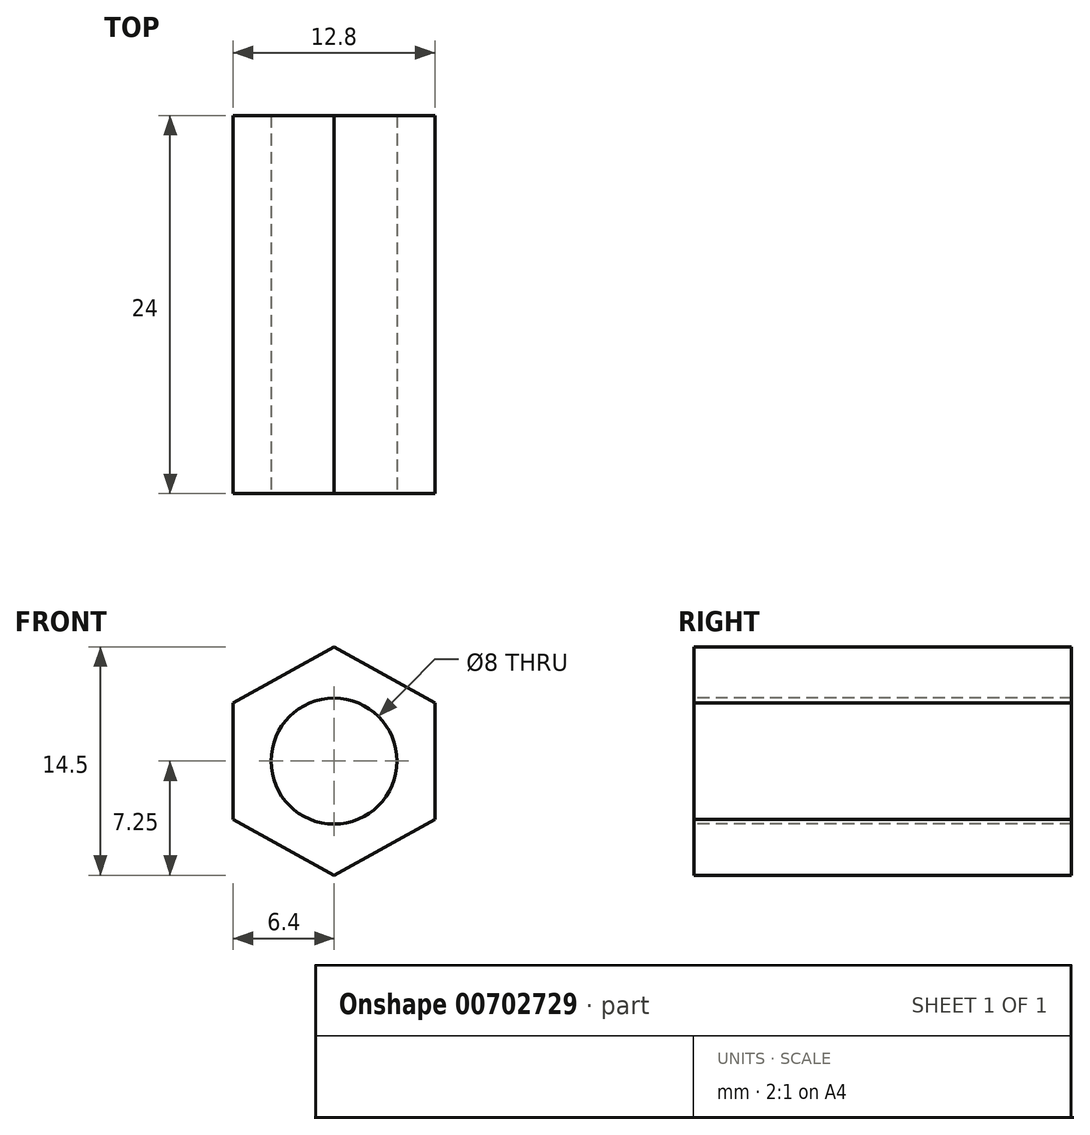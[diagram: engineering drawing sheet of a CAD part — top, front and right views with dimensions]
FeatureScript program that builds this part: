
annotation { "Feature Type Name" : "Feature", "Feature Type Description" : "" }
export const myFeature = defineFeature(function(context is Context, id is Id, definition is map)
    precondition{}
    {
        {
            var Q0;
            Q0=qCreatedBy(makeId("Front.planeOp"),FACE);
            var sketch = newSketch(context, id + "F0", { "sketchPlane" : qUnion([Q0])});
            skPoint(sketch, "E0.middle", {"position": v(0, 0) * mm});
            skLineSegment(sketch, "E1", {"start": v(-6.4, 3.7) * mm, "end": v(0, 7.25) * mm});
            skLineSegment(sketch, "E2", {"start": v(0, 7.25) * mm, "end": v(6.4, 3.7) * mm});
            skLineSegment(sketch, "E3", {"start": v(6.4, 3.7) * mm, "end": v(6.4, -3.7) * mm});
            skLineSegment(sketch, "E4", {"start": v(6.4, -3.7) * mm, "end": v(0, -7.25) * mm});
            skLineSegment(sketch, "E5", {"start": v(0, -7.25) * mm, "end": v(-6.4, -3.7) * mm});
            skLineSegment(sketch, "E6", {"start": v(-6.4, -3.7) * mm, "end": v(-6.4, 3.7) * mm});
            skSolve(sketch);
        }
        {
            var Q0;
            Q0=makeQuery(id+"F0.imprint","IMPRINT",FACE,{"disambiguationData":[TD([[makeQuery(id+"F0.imprint","IMPRINT",EDGE,{"derivedFrom":sQuery(id+"F0.wireOp",EDGE,"E2")}),-1.0]])]});
            extrude(context, id + "F1", {"entities" : qUnion([Q0]), "endBound" : BoundingType.SYMMETRIC, "depth" : 24 * mm, "offsetDistance" : 25 * mm});
        }
        {
            var Q0;
            Q0=makeQuery(id+"F1.opExtrude","CAP_FACE",FACE,{"disambiguationData":[OSD([sQuery(id+"F0.wireOp",EDGE,"E2"),sQuery(id+"F0.wireOp",EDGE,"E3"),sQuery(id+"F0.wireOp",EDGE,"E4"),sQuery(id+"F0.wireOp",EDGE,"E5"),sQuery(id+"F0.wireOp",EDGE,"E6"),sQuery(id+"F0.wireOp",EDGE,"E1")])],"isStart":false});
            var sketch = newSketch(context, id + "F2", { "sketchPlane" : qUnion([Q0])});
            skPoint(sketch, "E7", {"position": v(0, 0) * mm});
            skSolve(sketch);
        }
        {
            var Q0;
            Q0=sQuery(id+"F2.wireOp",VERTEX,"E7");
            var Q1;
            Q1=makeQuery(id+"F1.opExtrude","SWEPT_BODY",BODY,{"disambiguationData":[OSD([sQuery(id+"F0.wireOp",EDGE,"E2"),sQuery(id+"F0.wireOp",EDGE,"E3"),sQuery(id+"F0.wireOp",EDGE,"E4"),sQuery(id+"F0.wireOp",EDGE,"E5"),sQuery(id+"F0.wireOp",EDGE,"E6"),sQuery(id+"F0.wireOp",EDGE,"E1")])]});
            hole(context, id + "F3", {"style" : HoleStyle.SIMPLE, "endStyle" : HoleEndStyle.THROUGH, "holeDiameter" : 8 * mm, "majorDiameter" : 5 * mm, "isTappedThrough" : true, "tappedDepth" : 12 * mm, "tapClearance" : 3, "locations" : qUnion([Q0]), "scope" : qUnion([Q1])});
        }
    });
